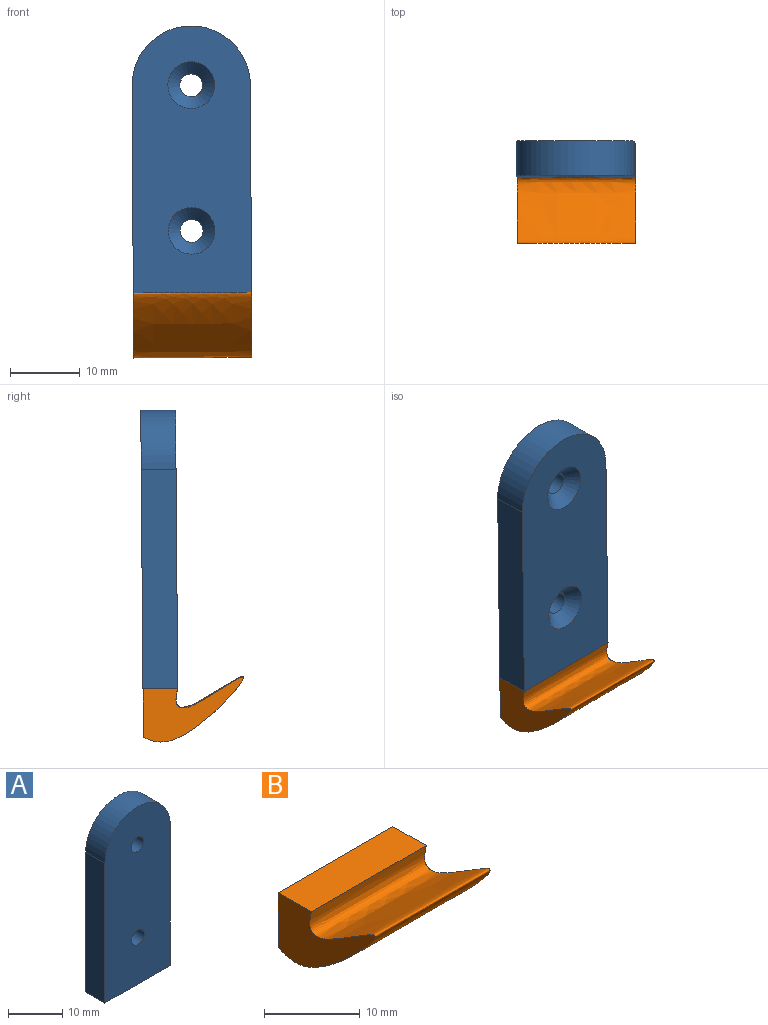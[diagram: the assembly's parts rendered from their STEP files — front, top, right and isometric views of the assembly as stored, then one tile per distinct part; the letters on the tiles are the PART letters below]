
ASSEMBLY  parts=2 mates=1
PART A: 10 faces, bbox 17x5x40 mm
  f0: plane 17x5mm, normal (0,0,-1), area 85mm2, adj f1,f3,f4,f5
  f1: plane 31.5x5mm, normal (1,0,0), area 157.5mm2, adj f0,f2,f4,f5
  f2: cylinder r=8.5mm len=17mm, axis (0,1,0), area 133.5mm2, adj f1,f3,f4,f5
  f3: plane 31.5x5mm, normal (-1,0,0), area 157.5mm2, adj f0,f2,f4,f5
  f4: plane 40x17mm, normal (0,-1,0), area 631.9mm2, adj f0,f1,f2,f3,f6,f8
  f5: plane 40x17mm, normal (0,1,0), area 578.1mm2, adj f0,f1,f2,f3,f7,f9
  f6: cylinder r=1.65mm len=3.3mm, axis (0,1,0), area 34.1mm2, adj f4,f7
  f7: cone r=1.65mm half-angle=45deg, axis (0,1,0), area 38.1mm2, adj f5,f6
  f8: cylinder r=1.65mm len=3.3mm, axis (0,1,0), area 34.1mm2, adj f4,f9
  f9: cone r=1.65mm half-angle=45deg, axis (0,1,0), area 38.1mm2, adj f5,f8
PART B: 5 faces, bbox 17x15.4x11.1 mm
  f0: extruded ~17x14.35mm, area 538.8mm2, adj f1,f2,f3,f4
  f1: plane 17x6.99mm, normal (0,1,0), area 118.8mm2, adj f0,f2,f3,f4
  f2: plane 17x4.94mm, normal (0,0.01,1), area 84mm2, adj f0,f1,f3,f4
  f3: plane 15.35x11.07mm, normal (1,0,0), area 62.1mm2, adj f0,f1,f2
  f4: plane 15.35x11.07mm, normal (-1,0,0), area 62.1mm2, adj f0,f1,f2
PLACE A rot(axis=(0,0,-1),180deg) t=(-3.53,0.51,-0.28)mm
PLACE B rot(axis=(0,-1,0.01),0.3deg) t=(-3.52,5.39,11.98)mm
MATE fastened A.f0 <-> B.f2  axis (0.01,-0.01,-1) through (-3.4,2.94,-10.24)mm
